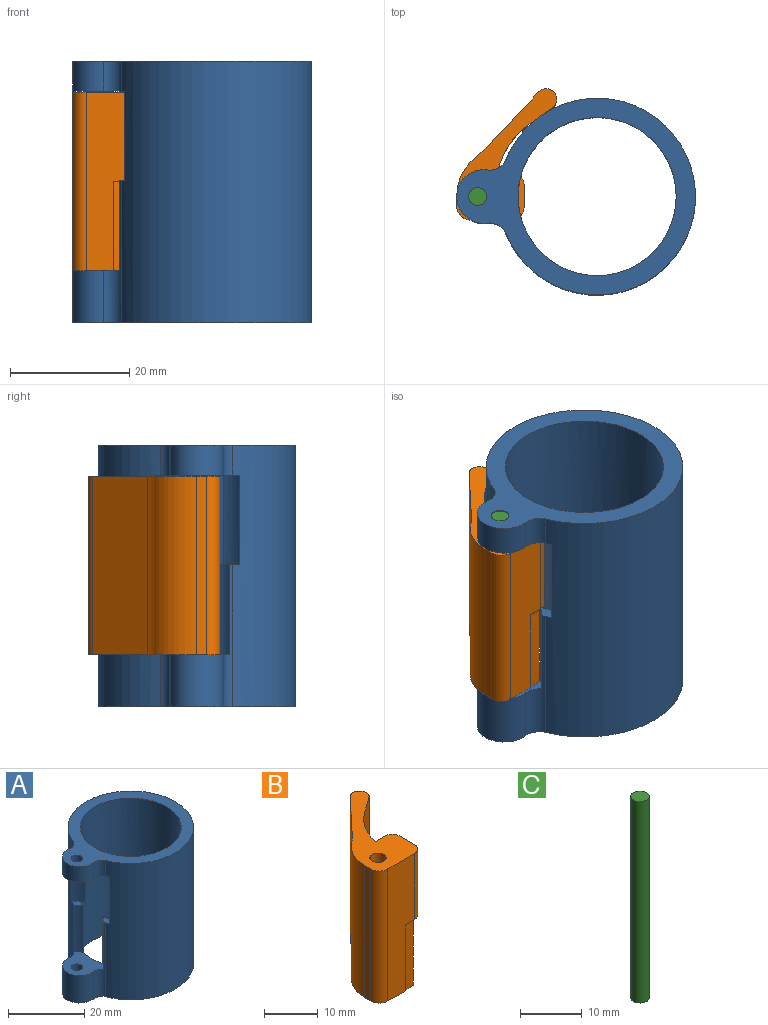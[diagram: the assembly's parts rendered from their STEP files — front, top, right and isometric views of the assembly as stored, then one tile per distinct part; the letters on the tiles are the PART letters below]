
ASSEMBLY  parts=3 mates=2
PART A: 23 faces, bbox 40.1x33x43.8 mm
  f0: cylinder r=2.95mm len=23.8mm, axis (0,0,-1), area 41.9mm2, adj f1,f6,f14,f18,f20,f22
  f1: cylinder r=4.5mm len=9mm, axis (0,0,-1), area 135.8mm2, adj f0,f2,f20,f22
  f2: cylinder r=2.95mm len=23.8mm, axis (0,0,-1), area 41.9mm2, adj f1,f6,f15,f19,f20,f22
  f3: cylinder r=1.5mm len=5.8mm, axis (0,0,-1), area 54.7mm2, adj f20,f21
  f4: cylinder r=13.25mm len=26.5mm, axis (0,0,-1), area 1527.4mm2, adj f11,f12,f13,f16,f17
  f5: cylinder r=14.5mm len=29mm, axis (0,0,-1), area 2058.4mm2, adj f12,f14,f15,f18,f19,f20,f22
  f6: cylinder r=16.5mm len=43.8mm, axis (0,0,-1), area 3963.2mm2, adj f0,f2,f7,f9,f11,f13,f14,f15
  f7: cylinder r=2.95mm len=5mm, axis (0,0,-1), area 18.4mm2, adj f6,f8,f11,f13
  f8: cylinder r=4.5mm len=9mm, axis (0,0,-1), area 77.2mm2, adj f7,f9,f11,f13
  f9: cylinder r=2.95mm len=5mm, axis (0,0,-1), area 18.4mm2, adj f6,f8,f11,f13
  f10: cylinder r=1.5mm len=5mm, axis (0,0,-1), area 47.1mm2, adj f11,f13
  f11: plane 40.05x33mm, normal (0,0,1), area 354.4mm2, adj f4,f6,f7,f8,f9,f10
  f12: plane 29x27.83mm, normal (0,0,-1), area 95.8mm2, adj f4,f5,f16,f17
  f13: plane 14.27x11.09mm, normal (0,0,-1), area 90.5mm2, adj f4,f6,f7,f8,f9,f10,f16,f17
  f14: plane 3.51x2.37mm, normal (0,0,1), area 4mm2, adj f0,f5,f6,f16,f18
  f15: plane 3.51x2.37mm, normal (0,0,1), area 4mm2, adj f2,f5,f6,f17,f19
  f16: cylinder r=8.8mm len=15mm, axis (0,0,-1), area 54mm2, adj f4,f6,f12,f13,f14
  f17: cylinder r=8.8mm len=15mm, axis (0,0,-1), area 54mm2, adj f4,f6,f12,f13,f15
  f18: cylinder r=7mm len=15mm, axis (0,0,1), area 37.8mm2, adj f0,f5,f14,f20
  f19: cylinder r=7mm len=15mm, axis (0,0,1), area 37.8mm2, adj f2,f5,f15,f20
  f20: plane 11.01x9.51mm, normal (0,0,1), area 69.3mm2, adj f0,f1,f2,f3,f5,f18,f19
  f21: plane 3x3mm, normal (0,0,1), area 7.1mm2, adj f3
  f22: plane 40.05x33mm, normal (0,0,-1), area 252.5mm2, adj f0,f1,f2,f5,f6
PART B: 18 faces, bbox 16.8x22.2x30 mm
  f0: plane 30x3.93mm, normal (0.58,-0.81,0), area 145.2mm2, adj f1,f10,f11,f16
  f1: cylinder r=1.75mm len=30mm, axis (0,0,1), area 175.3mm2, adj f0,f2,f11,f16
  f2: plane 30x9.35mm, normal (-0.73,0.69,0), area 385.2mm2, adj f1,f3,f11,f16
  f3: cylinder r=10.65mm len=30mm, axis (0,0,1), area 57.9mm2, adj f2,f4,f11,f16
  f4: cylinder r=8.59mm len=30mm, axis (0,0,1), area 241.4mm2, adj f3,f5,f11,f16
  f5: plane 30x1.59mm, normal (-1,0,0), area 47.8mm2, adj f4,f6,f11,f16
  f6: cylinder r=2.25mm len=30mm, axis (0,0,1), area 105.8mm2, adj f5,f7,f11,f16
  f7: plane 30x7.02mm, normal (0,-1,0), area 173.6mm2, adj f6,f8,f11,f12,f16,f17
  f8: extruded ~15x7.84mm, area 185.8mm2, adj f7,f10,f11,f17
  f9: cylinder r=1.5mm len=30mm, axis (0,0,1), area 282.7mm2, adj f11,f16
  f10: cylinder r=13.42mm len=30mm, axis (0,0,1), area 297.5mm2, adj f0,f8,f11,f15,f16
  f11: plane 22.18x16.77mm, normal (0,0,-1), area 122.6mm2, adj f0,f1,f2,f3,f4,f5,f6,f7
  f12: cylinder r=2mm len=15mm, axis (0,0,-1), area 47.3mm2, adj f7,f13,f16,f17
  f13: plane 15x3.84mm, normal (1,0,0), area 57.6mm2, adj f12,f14,f16,f17
  f14: cylinder r=2mm len=15mm, axis (0,0,-1), area 47.1mm2, adj f13,f15,f16,f17
  f15: plane 15x2.48mm, normal (0,1,0), area 37.2mm2, adj f10,f14,f16,f17
  f16: plane 21.94x16.77mm, normal (0,0,1), area 133.3mm2, adj f0,f1,f2,f3,f4,f5,f6,f7
  f17: plane 8.31x4.48mm, normal (0,0,-1), area 10.8mm2, adj f7,f8,f12,f13,f14,f15
PART C: 3 faces, bbox 3x3x40 mm
  f0: cylinder r=1.5mm len=40mm, axis (0,0,-1), area 377mm2, adj f1,f2
  f1: plane 3x3mm, normal (0,0,1), area 7.1mm2, adj f0
  f2: plane 3x3mm, normal (0,0,-1), area 7.1mm2, adj f0
PLACE A rot(axis=(-0.08,0.97,-0.23),0deg) t=(12.67,-0.42,0)mm
PLACE B rot(axis=(-0.08,0.97,-0.23),0deg) t=(12.67,-0.42,-0.14)mm
PLACE C rot(axis=(-0.08,0.97,-0.23),0deg) t=(12.67,-0.42,-0.14)mm
MATE revolute B.f9 <-> C.f0  axis (0,0,1) through (12.67,-0.42,14.86)mm
MATE slider C.f0 <-> A.f3  axis (0,0,-1) through (12.67,-0.42,19.86)mm
